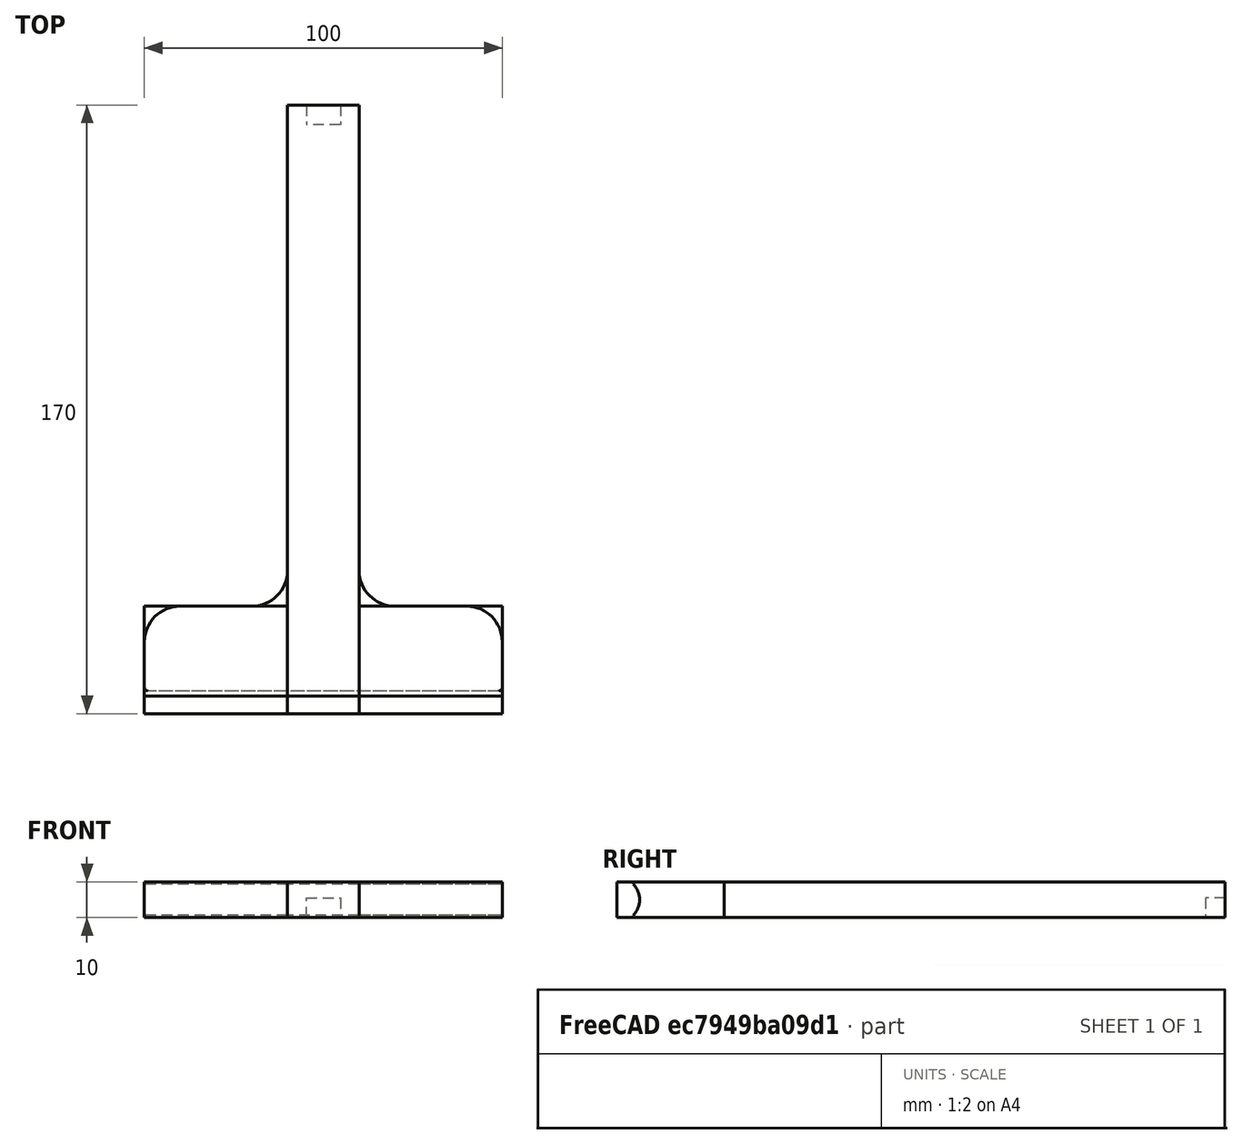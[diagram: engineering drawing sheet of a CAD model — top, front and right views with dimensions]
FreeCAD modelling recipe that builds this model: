
FCSTD DOCUMENT  (FreeCAD 0.16R)
Label: 26-50mmFauxRoue2
License: All rights reserved
LicenseURL: http://en.wikipedia.org/wiki/All_rights_reserved
objects: Sketcher::SketchObject×5, PartDesign::Fillet×3, PartDesign::Pad×2, PartDesign::Pocket×2, Mesh::Feature×2, PartDesign::Chamfer×1
note: 17 computed .brp shape members not serialized (recipe doc carries the construction recipe); baked Part::Feature solids carry a one-line shape summary decoded from their .brp

FEATURE [Sketcher::SketchObject] Sketch
FEATURE [Sketcher::SketchObject] Sketch001
  sketch-geometry (4):
    g0: LineSegment StartX=-10 StartY=170 StartZ=0 EndX=10 EndY=170 EndZ=0
    g1: LineSegment StartX=10 StartY=170 StartZ=0 EndX=10 EndY=0 EndZ=0
    g2: LineSegment StartX=10 StartY=0 StartZ=0 EndX=-10 EndY=0 EndZ=0
    g3: LineSegment StartX=-10 StartY=0 StartZ=0 EndX=-10 EndY=170 EndZ=0
  constraints (12):
    c: Coincident(g0,g1)
    c: Coincident(g1,g2)
    c: Coincident(g2,g3)
    c: Coincident(g3,g0)
    c: Horizontal(g0)
    c: Horizontal(g2)
    c: Vertical(g1)
    c: Vertical(g3)
    c: PointOnObject(g1,g-1)
    c: Symmetric(g1,g2,g-2)
    c: Distance(g0) = 20
    c: Distance(g1) = 170
FEATURE [PartDesign::Pad] Pad
  Length = 10
  Length2 = 100
  Sketch = -> Sketch001
  Type = 0
FEATURE [Sketcher::SketchObject] Sketch002
  Placement = pos=(0,0,10) rot=(0,0,1;0rad)
  Support = -> Pad [Face6]
  sketch-geometry (4):
    g0: LineSegment StartX=-50 StartY=30 StartZ=0 EndX=50 EndY=30 EndZ=0
    g1: LineSegment StartX=50 StartY=30 StartZ=0 EndX=50 EndY=0 EndZ=0
    g2: LineSegment StartX=50 StartY=0 StartZ=0 EndX=-50 EndY=0 EndZ=0
    g3: LineSegment StartX=-50 StartY=0 StartZ=0 EndX=-50 EndY=30 EndZ=0
  constraints (12):
    c: Coincident(g0,g1)
    c: Coincident(g1,g2)
    c: Coincident(g2,g3)
    c: Coincident(g3,g0)
    c: Horizontal(g0)
    c: Horizontal(g2)
    c: Vertical(g1)
    c: Vertical(g3)
    c: PointOnObject(g1,g-1)
    c: Symmetric(g1,g2,g-2)
    c: Distance(g0) = 100
    c: Distance(g1) = 30
FEATURE [PartDesign::Pad] Pad001
  Length = 10
  Length2 = 100
  Reversed = true
  Sketch = -> Sketch002
  Type = 0
FEATURE [Sketcher::SketchObject] Sketch003
  Placement = pos=(-50,0,0) rot=(0.57735,-0.57735,-0.57735;2.0944rad)
  Support = -> Pad001 [Face12]
  sketch-geometry (1):
    g0: Circle CenterX=0 CenterY=5 CenterZ=0 NormalX=0 NormalY=0 NormalZ=1 Radius=6.35
  constraints (3):
    c: Radius(g0) = 6.35
    c: PointOnObject(g0,g-2)
    c: DistanceY(g0) = 5
FEATURE [PartDesign::Pocket] Pocket
  Length = 5
  Sketch = -> Sketch003
  Type = 1
FEATURE [PartDesign::Chamfer] Chamfer
  Base = -> Pocket [Edge34,Edge30]
  Size = 1
FEATURE [Sketcher::SketchObject] Sketch004
  Placement = pos=(0,170,0) rot=(0,0.707107,0.707107;3.14159rad)
  Support = -> Chamfer [Face13]
  sketch-geometry (4):
    g0: LineSegment StartX=-4.75 StartY=0 StartZ=0 EndX=4.75 EndY=0 EndZ=0
    g1: LineSegment StartX=4.75 StartY=0 StartZ=0 EndX=4.75 EndY=5.5 EndZ=0
    g2: LineSegment StartX=4.75 StartY=5.5 StartZ=0 EndX=-4.75 EndY=5.5 EndZ=0
    g3: LineSegment StartX=-4.75 StartY=5.5 StartZ=0 EndX=-4.75 EndY=0 EndZ=0
  constraints (12):
    c: Coincident(g0,g1)
    c: Coincident(g1,g2)
    c: Coincident(g2,g3)
    c: Coincident(g3,g0)
    c: Horizontal(g0)
    c: Horizontal(g2)
    c: Vertical(g1)
    c: Vertical(g3)
    c: Symmetric(g0,g0,g-2)
    c: Distance(g1) = 5.5
    c: PointOnObject(g0,g-1)
    c: Distance(g2) = 9.5
FEATURE [PartDesign::Pocket] Pocket001
  Length = 5.5
  Sketch = -> Sketch004
  Type = 0
FEATURE [PartDesign::Fillet] Fillet
  Base = -> Pocket001 [Edge24,Edge25,Edge50,Edge48]
  Radius = 10
FEATURE [PartDesign::Fillet] Fillet001
  Base = -> Fillet [Edge26]
  Radius = 1
FEATURE [PartDesign::Fillet] Fillet002
  Base = -> Fillet001 [Edge41]
  Radius = 1
FEATURE [Mesh::Feature] Mesh  label="Fillet002 (Meshed)"
FEATURE [Mesh::Feature] Mesh001  label="Fillet002 (Meshed)001"
